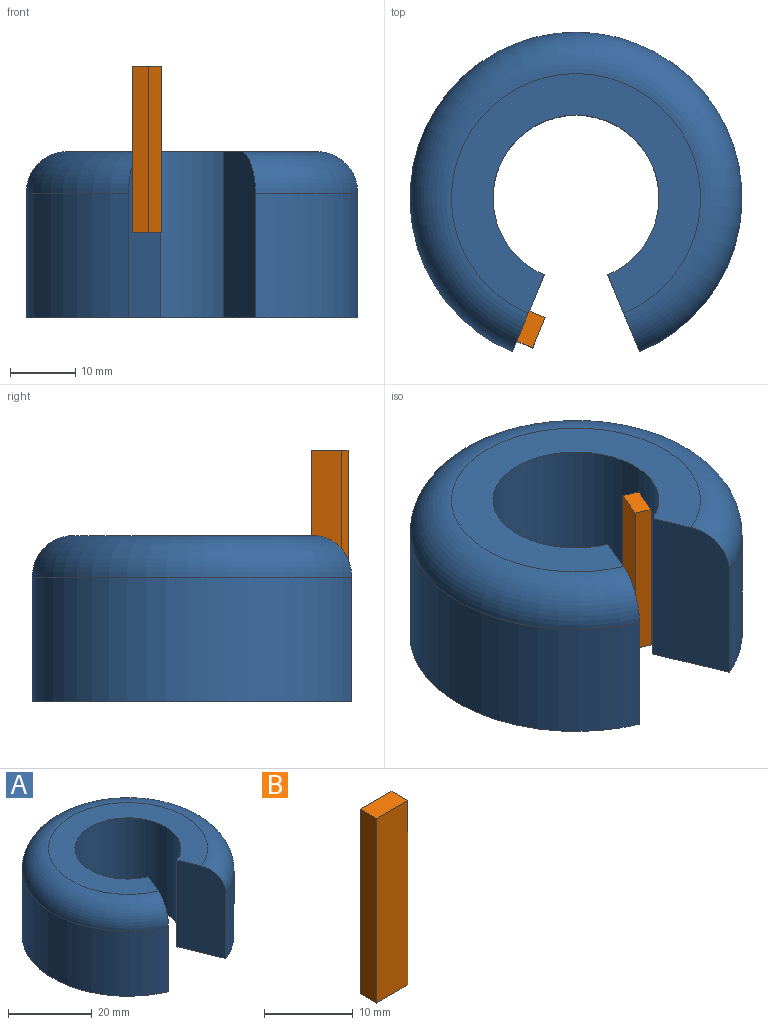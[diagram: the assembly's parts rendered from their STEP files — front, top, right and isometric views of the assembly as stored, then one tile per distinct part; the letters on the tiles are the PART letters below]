
ASSEMBLY  parts=2 mates=1
PART A: 7 faces, bbox 55x52.9x25.4 mm
  f0: plane 25.4x11.73mm, normal (0.92,-0.38,0), area 313.9mm2, adj f1,f3,f4,f5,f6
  f1: cylinder r=12.7mm len=25.4mm, axis (0,0,-1), area 1773.5mm2, adj f0,f2,f4,f5
  f2: plane 25.4x11.73mm, normal (-0.92,-0.38,0), area 313.9mm2, adj f1,f3,f4,f5,f6
  f3: cylinder r=25.4mm len=50.8mm, axis (0,0,-1), area 2660.2mm2, adj f0,f2,f5,f6
  f4: plane 38.1x36.65mm, normal (0,0,1), area 554.2mm2, adj f0,f1,f2,f6
  f5: plane 50.8x48.87mm, normal (0,0,-1), area 1330.1mm2, adj f0,f1,f2,f3
  f6: torus R=19.05mm, axis (0,0,1), area 1266.3mm2, adj f0,f2,f3,f4
PART B: 6 faces, bbox 5x2.6x25.4 mm
  f0: plane 25.4x5mm, normal (0,-1,0), area 127mm2, adj f1,f3,f4,f5
  f1: plane 25.4x2.64mm, normal (1,0,0), area 66.9mm2, adj f0,f2,f4,f5
  f2: plane 25.4x5mm, normal (0,1,0), area 127mm2, adj f1,f3,f4,f5
  f3: plane 25.4x2.64mm, normal (-1,0,0), area 66.9mm2, adj f0,f2,f4,f5
  f4: plane 5x2.64mm, normal (0,0,1), area 13.2mm2, adj f0,f1,f2,f3
  f5: plane 5x2.64mm, normal (0,0,-1), area 13.2mm2, adj f0,f1,f2,f3
PLACE A t=(-11.04,4.57,0)mm fixed
PLACE B rot(axis=(0.83,0.56,0),180deg) t=(-17.93,-15.52,25.72)mm
MATE planar B.f0 <-> A.f0  axis (-0.92,0.38,0) through (-18.19,-12.7,0.32)mm
